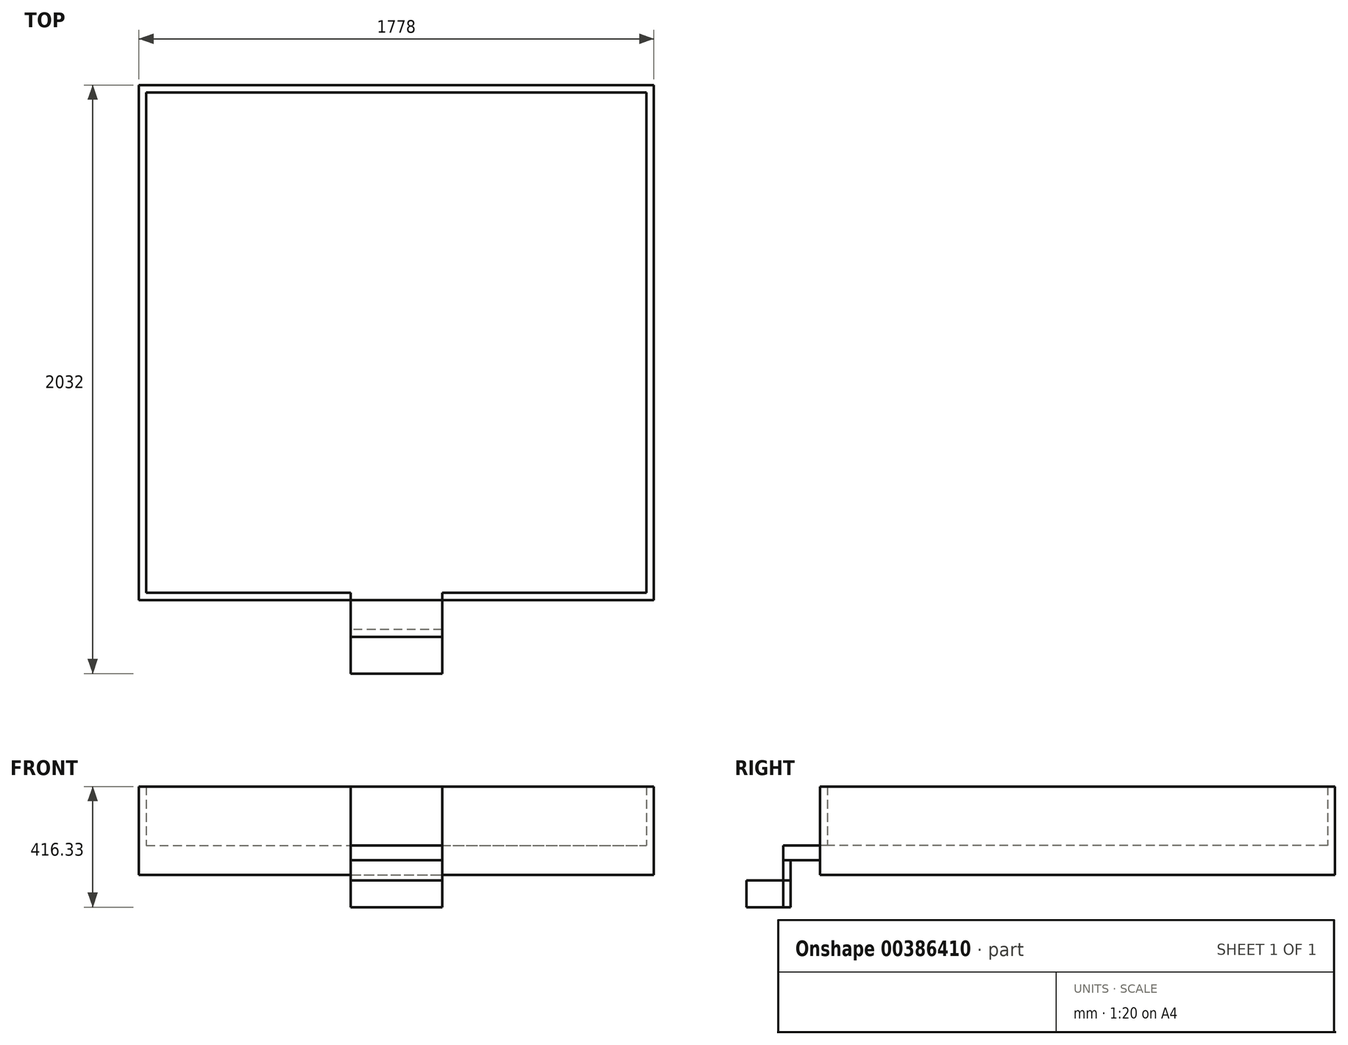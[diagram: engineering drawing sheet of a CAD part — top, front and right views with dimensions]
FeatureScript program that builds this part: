
annotation { "Feature Type Name" : "Feature", "Feature Type Description" : "" }
export const myFeature = defineFeature(function(context is Context, id is Id, definition is map)
    precondition{}
    {
        {
            var Q0;
            Q0=qCreatedBy(makeId("Top.planeOp"),FACE);
            var sketch = newSketch(context, id + "F0", { "sketchPlane" : qUnion([Q0])});
            skLineSegment(sketch, "E0.bottom", {"start": v(-889, 889) * mm, "end": v(889, 889) * mm});
            skLineSegment(sketch, "E0.top", {"start": v(-889, -889) * mm, "end": v(889, -889) * mm});
            skLineSegment(sketch, "E0.left", {"start": v(-889, 889) * mm, "end": v(-889, -889) * mm});
            skLineSegment(sketch, "E0.right", {"start": v(889, 889) * mm, "end": v(889, -889) * mm});
            skPoint(sketch, "E0.middle", {"position": v(0, 0) * mm});
            skSolve(sketch);
        }
        {
            var Q0;
            Q0 = qSketchRegion(id + "F0", true);
            extrude(context, id + "F1", {"entities" : qUnion([Q0]), "depth" : 25.4 * mm});
        }
        {
            var Q0;
            Q0=makeQuery(id+"F1.opExtrude","CAP_FACE",FACE,{"disambiguationData":[OSD([sQuery(id+"F0.wireOp",EDGE,"E0.bottom"),sQuery(id+"F0.wireOp",EDGE,"E0.top"),sQuery(id+"F0.wireOp",EDGE,"E0.left"),sQuery(id+"F0.wireOp",EDGE,"E0.right")])],"isStart":false});
            var sketch = newSketch(context, id + "F2", { "sketchPlane" : qUnion([Q0])});
            skLineSegment(sketch, "E1.0", {"start": v(-889, 889) * mm, "end": v(889, 889) * mm});
            skLineSegment(sketch, "E1.1", {"start": v(-889, 889) * mm, "end": v(-889, -889) * mm});
            skLineSegment(sketch, "E1.2", {"start": v(-889, -889) * mm, "end": v(889, -889) * mm});
            skLineSegment(sketch, "E1.3", {"start": v(889, 889) * mm, "end": v(889, -889) * mm});
            skLineSegment(sketch, "E2.0", {"start": v(-863.6, 863.6) * mm, "end": v(863.6, 863.6) * mm});
            skLineSegment(sketch, "E2.1", {"start": v(-863.6, 863.6) * mm, "end": v(-863.6, -863.6) * mm});
            skLineSegment(sketch, "E2.2", {"start": v(-863.6, -863.6) * mm, "end": v(863.6, -863.6) * mm});
            skLineSegment(sketch, "E2.3", {"start": v(863.6, 863.6) * mm, "end": v(863.6, -863.6) * mm});
            skSolve(sketch);
        }
        {
            var Q0;
            Q0=makeQuery(id+"F2.imprint","IMPRINT",FACE,{"disambiguationData":[TD([[makeQuery(id+"F2.imprint","IMPRINT",EDGE,{"derivedFrom":sQuery(id+"F2.wireOp",EDGE,"E1.0")}),-1.0]])]});
            extrude(context, id + "F3", {"entities" : qUnion([Q0]), "depth" : 203.2 * mm});
        }
        {
            var Q0;
            Q0=makeQuery(id+"F3.opExtrude","SWEPT_FACE",FACE,{"disambiguationData":[OSD([sQuery(id+"F2.wireOp",EDGE,"E1.2")])]});
            var sketch = newSketch(context, id + "F4", { "sketchPlane" : qUnion([Q0])});
            skPoint(sketch, "E3.0", {"position": v(0, 25.4) * mm});
            skLineSegment(sketch, "E4", {"start": v(0, 25.4) * mm, "end": v(0, 228.6) * mm, "construction": true});
            skLineSegment(sketch, "E5.bottom", {"start": v(-157.93, 228.6) * mm, "end": v(157.93, 228.6) * mm});
            skLineSegment(sketch, "E5.top", {"start": v(-157.93, 25.4) * mm, "end": v(157.93, 25.4) * mm});
            skLineSegment(sketch, "E5.left", {"start": v(-157.93, 228.6) * mm, "end": v(-157.93, 25.4) * mm});
            skLineSegment(sketch, "E5.right", {"start": v(157.93, 228.6) * mm, "end": v(157.93, 25.4) * mm});
            skPoint(sketch, "E5.middle", {"position": v(0, 127) * mm});
            skSolve(sketch);
        }
        {
            var Q0;
            Q0 = qSketchRegion(id + "F4", true);
            extrude(context, id + "F5", {"entities" : qUnion([Q0]), "operationType" : NewBodyOperationType.REMOVE, "oppositeDirection" : true, "depth" : 25.4 * mm});
        }
        {
            var Q0;
            Q0=makeQuery(id+"F1.opExtrude","SWEPT_BODY",BODY,{"disambiguationData":[OSD([sQuery(id+"F0.wireOp",EDGE,"E0.bottom"),sQuery(id+"F0.wireOp",EDGE,"E0.top"),sQuery(id+"F0.wireOp",EDGE,"E0.left"),sQuery(id+"F0.wireOp",EDGE,"E0.right")])]});
            var Q1;
            Q1=makeQuery(id+"F3.opExtrude","SWEPT_BODY",BODY,{"disambiguationData":[OSD([sQuery(id+"F2.wireOp",EDGE,"E1.0"),sQuery(id+"F2.wireOp",EDGE,"E1.1"),sQuery(id+"F2.wireOp",EDGE,"E1.2"),sQuery(id+"F2.wireOp",EDGE,"E1.3"),sQuery(id+"F2.wireOp",EDGE,"E2.0"),sQuery(id+"F2.wireOp",EDGE,"E2.1"),sQuery(id+"F2.wireOp",EDGE,"E2.2"),sQuery(id+"F2.wireOp",EDGE,"E2.3")])]});
            booleanBodies(context, id + "F6", {"operationType" : BooleanOperationType.UNION, "tools" : qUnion([Q0, Q1])});
        }
        {
            var Q0;
            Q0=makeQuery(id+"F1.opExtrude","CAP_FACE",FACE,{"disambiguationData":[OSD([sQuery(id+"F0.wireOp",EDGE,"E0.bottom"),sQuery(id+"F0.wireOp",EDGE,"E0.top"),sQuery(id+"F0.wireOp",EDGE,"E0.left"),sQuery(id+"F0.wireOp",EDGE,"E0.right")])],"isStart":true});
            extrude(context, id + "F7", {"entities" : qUnion([Q0]), "operationType" : NewBodyOperationType.ADD, "depth" : 76.2 * mm});
        }
        {
            var Q0;
            {var subQ0=sQuery(id+"F0.wireOp",EDGE,"E0.top");var subQ5=sQuery(id+"F2.wireOp",EDGE,"E1.3");var subQ6=sQuery(id+"F2.wireOp",EDGE,"E1.2");var subQ7=sQuery(id+"F2.wireOp",EDGE,"E1.1");var subQ11=makeQuery(id+"F3.opExtrude","SWEPT_FACE",FACE,{"disambiguationData":[OSD([subQ6])]});Q0=makeQuery(id+"F7.boolean.opBoolean","MERGE",FACE,{"derivedFrom":[makeQuery(id+"F6.opBoolean","MERGE",FACE,{"derivedFrom":[makeQuery(id+"F1.opExtrude","SWEPT_FACE",FACE,{"disambiguationData":[OSD([subQ0])]}),makeQuery(id+"F5.boolean.opBoolean","SPLIT",FACE,{"disambiguationData":[TD([makeQuery(id+"F3.opExtrude","SWEPT_FACE",FACE,{"disambiguationData":[OSD([subQ7])]})])],"derivedFrom":subQ11}),makeQuery(id+"F5.boolean.opBoolean","SPLIT",FACE,{"disambiguationData":[TD([makeQuery(id+"F3.opExtrude","SWEPT_FACE",FACE,{"disambiguationData":[OSD([subQ5])]})])],"derivedFrom":subQ11})]}),makeQuery(id+"F7.opExtrude","SWEPT_FACE",FACE,{"disambiguationData":[OSD([subQ0])]})]});}
            var sketch = newSketch(context, id + "F8", { "sketchPlane" : qUnion([Q0])});
            skLineSegment(sketch, "E6.bottom", {"start": v(-157.93, 25.4) * mm, "end": v(157.93, 25.4) * mm});
            skLineSegment(sketch, "E6.top", {"start": v(-157.93, -25.43) * mm, "end": v(157.93, -25.43) * mm});
            skLineSegment(sketch, "E6.left", {"start": v(-157.93, 25.4) * mm, "end": v(-157.93, -25.43) * mm});
            skLineSegment(sketch, "E6.right", {"start": v(157.93, 25.4) * mm, "end": v(157.93, -25.43) * mm});
            skSolve(sketch);
        }
        {
            var Q0;
            Q0 = qSketchRegion(id + "F8", true);
            extrude(context, id + "F9", {"entities" : qUnion([Q0]), "depth" : 127 * mm});
        }
        {
            var Q0;
            Q0=makeQuery(id+"F9.opExtrude","CAP_FACE",FACE,{"disambiguationData":[OSD([sQuery(id+"F8.wireOp",EDGE,"E6.bottom"),sQuery(id+"F8.wireOp",EDGE,"E6.top"),sQuery(id+"F8.wireOp",EDGE,"E6.left"),sQuery(id+"F8.wireOp",EDGE,"E6.right")])],"isStart":false});
            var sketch = newSketch(context, id + "F10", { "sketchPlane" : qUnion([Q0])});
            skLineSegment(sketch, "E7.bottom", {"start": v(-157.93, -25.43) * mm, "end": v(157.93, -25.43) * mm});
            skLineSegment(sketch, "E7.top", {"start": v(-157.93, -94.88) * mm, "end": v(157.93, -94.88) * mm});
            skLineSegment(sketch, "E7.left", {"start": v(-157.93, -25.43) * mm, "end": v(-157.93, -94.88) * mm});
            skLineSegment(sketch, "E7.right", {"start": v(157.93, -25.43) * mm, "end": v(157.93, -94.88) * mm});
            skSolve(sketch);
        }
        {
            var Q0;
            Q0 = qSketchRegion(id + "F10", true);
            extrude(context, id + "F11", {"entities" : qUnion([Q0]), "oppositeDirection" : true, "depth" : 25.4 * mm});
        }
        {
            var Q0;
            Q0=makeQuery(id+"F11.opExtrude","CAP_FACE",FACE,{"disambiguationData":[OSD([sQuery(id+"F10.wireOp",EDGE,"E7.bottom"),sQuery(id+"F10.wireOp",EDGE,"E7.top"),sQuery(id+"F10.wireOp",EDGE,"E7.left"),sQuery(id+"F10.wireOp",EDGE,"E7.right")])],"isStart":true});
            var sketch = newSketch(context, id + "F12", { "sketchPlane" : qUnion([Q0])});
            skLineSegment(sketch, "E8.bottom", {"start": v(-157.93, -94.88) * mm, "end": v(157.93, -94.88) * mm});
            skLineSegment(sketch, "E8.top", {"start": v(-157.93, -187.73) * mm, "end": v(157.93, -187.73) * mm});
            skLineSegment(sketch, "E8.left", {"start": v(-157.93, -94.88) * mm, "end": v(-157.93, -187.73) * mm});
            skLineSegment(sketch, "E8.right", {"start": v(157.93, -94.88) * mm, "end": v(157.93, -187.73) * mm});
            skSolve(sketch);
        }
        {
            var Q0;
            Q0 = qSketchRegion(id + "F12", true);
            extrude(context, id + "F13", {"entities" : qUnion([Q0]), "depth" : 127 * mm});
        }
        {
            var Q0;
            Q0=makeQuery(id+"F13.opExtrude","CAP_FACE",FACE,{"disambiguationData":[OSD([sQuery(id+"F12.wireOp",EDGE,"E8.bottom"),sQuery(id+"F12.wireOp",EDGE,"E8.top"),sQuery(id+"F12.wireOp",EDGE,"E8.left"),sQuery(id+"F12.wireOp",EDGE,"E8.right")])],"isStart":false});
            var sketch = newSketch(context, id + "F14", { "sketchPlane" : qUnion([Q0])});
            skLineSegment(sketch, "E9", {"start": v(-730.41, -187.73) * mm, "end": v(793.59, -187.73) * mm});
            skSolve(sketch);
        }
        {
            var Q0;
            Q0=sQuery(id+"F14.wireOp",EDGE,"E9");
            extrude(context, id + "F15", {"bodyType" : ToolBodyType.SURFACE, "surfaceEntities" : qUnion([Q0]), "oppositeDirection" : true, "depth" : 1778 * mm});
        }
        {
            var Q0;
            Q0=makeQuery(id+"F11.opExtrude","SWEPT_FACE",FACE,{"disambiguationData":[OSD([sQuery(id+"F10.wireOp",EDGE,"E7.top")])]});
            var Q1;
            Q1=makeQuery(id+"F15.opExtrude","SWEPT_FACE",FACE,{"disambiguationData":[OSD([sQuery(id+"F14.wireOp",EDGE,"E9")])]});
            extrude(context, id + "F16", {"entities" : qUnion([Q0]), "endBound" : BoundingType.UP_TO_SURFACE, "endBoundEntityFace" : qUnion([Q1]), "depth" : 25.4 * mm});
        }
        {
            var Q0;
            Q0=makeQuery(id+"F1.opExtrude","CAP_FACE",FACE,{"disambiguationData":[OSD([sQuery(id+"F0.wireOp",EDGE,"E0.bottom"),sQuery(id+"F0.wireOp",EDGE,"E0.top"),sQuery(id+"F0.wireOp",EDGE,"E0.left"),sQuery(id+"F0.wireOp",EDGE,"E0.right")])],"isStart":false});
            var sketch = newSketch(context, id + "F17", { "sketchPlane" : qUnion([Q0])});
            skLineSegment(sketch, "E10.bottom", {"start": v(-571.5, 571.5) * mm, "end": v(571.5, 571.5) * mm});
            skLineSegment(sketch, "E10.top", {"start": v(-571.5, -571.5) * mm, "end": v(571.5, -571.5) * mm});
            skLineSegment(sketch, "E10.left", {"start": v(-571.5, 571.5) * mm, "end": v(-571.5, -571.5) * mm});
            skLineSegment(sketch, "E10.right", {"start": v(571.5, 571.5) * mm, "end": v(571.5, -571.5) * mm});
            skPoint(sketch, "E10.middle", {"position": v(0, 0) * mm});
            skSolve(sketch);
        }
    });
